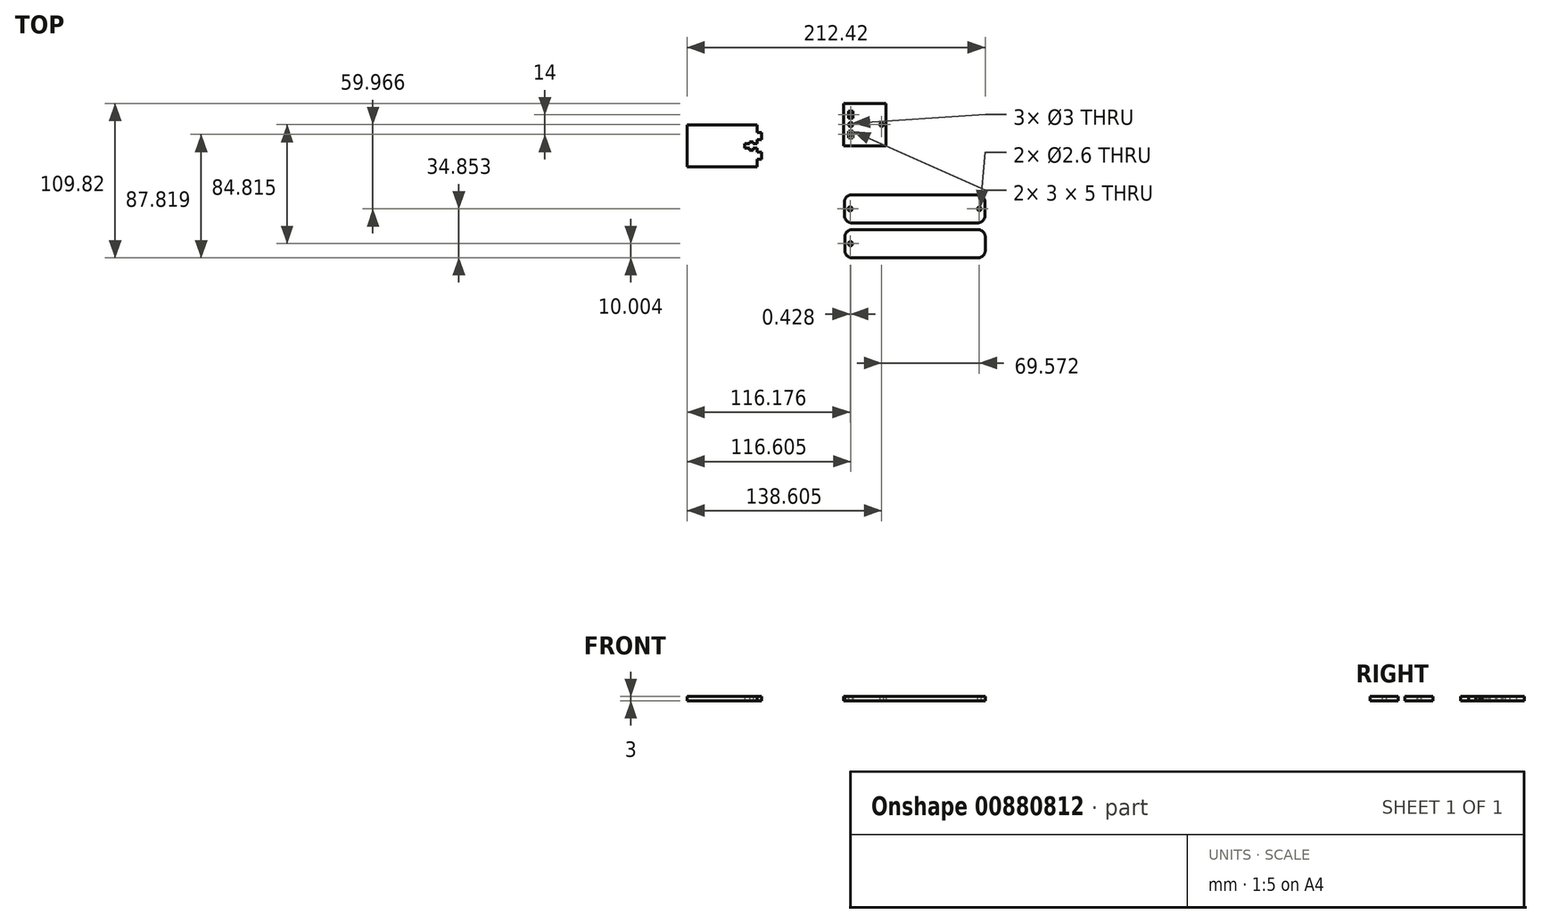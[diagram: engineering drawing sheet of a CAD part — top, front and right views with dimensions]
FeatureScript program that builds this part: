
annotation { "Feature Type Name" : "Feature", "Feature Type Description" : "" }
export const myFeature = defineFeature(function(context is Context, id is Id, definition is map)
    precondition{}
    {
        {
            var Q0;
            Q0=qCreatedBy(makeId("Top.planeOp"),FACE);
            var sketch = newSketch(context, id + "F0", { "sketchPlane" : qUnion([Q0])});
            skLineSegment(sketch, "E0", {"start": v(-41.94, 24.5) * mm, "end": v(-38.94, 24.5) * mm});
            skLineSegment(sketch, "E1", {"start": v(-38.94, 24.5) * mm, "end": v(-38.94, 19.5) * mm});
            skLineSegment(sketch, "E2", {"start": v(-38.94, 19.5) * mm, "end": v(-41.94, 19.5) * mm});
            skLineSegment(sketch, "E3", {"start": v(-41.94, 19.5) * mm, "end": v(-41.94, 16.5) * mm});
            skLineSegment(sketch, "E4", {"start": v(-41.94, 16.5) * mm, "end": v(-44.94, 16.5) * mm});
            skLineSegment(sketch, "E5", {"start": v(-44.94, 16.5) * mm, "end": v(-44.94, 18) * mm});
            skLineSegment(sketch, "E6", {"start": v(-44.94, 18) * mm, "end": v(-47.44, 18) * mm});
            skLineSegment(sketch, "E7", {"start": v(-47.44, 18) * mm, "end": v(-47.44, 16.5) * mm});
            skLineSegment(sketch, "E8", {"start": v(-47.44, 16.5) * mm, "end": v(-50.94, 16.5) * mm});
            skLineSegment(sketch, "E9", {"start": v(-50.94, 16.5) * mm, "end": v(-50.94, 13.5) * mm});
            skLineSegment(sketch, "E10", {"start": v(-50.94, 13.5) * mm, "end": v(-47.44, 13.5) * mm});
            skLineSegment(sketch, "E11", {"start": v(-47.44, 13.5) * mm, "end": v(-47.44, 12) * mm});
            skLineSegment(sketch, "E12", {"start": v(-47.44, 12) * mm, "end": v(-44.94, 12) * mm});
            skLineSegment(sketch, "E13", {"start": v(-44.94, 12) * mm, "end": v(-44.94, 13.5) * mm});
            skLineSegment(sketch, "E14", {"start": v(-44.94, 13.5) * mm, "end": v(-41.94, 13.5) * mm});
            skLineSegment(sketch, "E15", {"start": v(-41.94, 13.5) * mm, "end": v(-41.94, 10.5) * mm});
            skLineSegment(sketch, "E16", {"start": v(-41.94, 10.5) * mm, "end": v(-38.94, 10.5) * mm});
            skLineSegment(sketch, "E17", {"start": v(-38.94, 10.5) * mm, "end": v(-38.94, 5.5) * mm});
            skLineSegment(sketch, "E18", {"start": v(-38.94, 5.5) * mm, "end": v(-41.94, 5.5) * mm});
            skLineSegment(sketch, "E19.bottom", {"start": v(-91.94, 30) * mm, "end": v(-41.94, 30) * mm});
            skLineSegment(sketch, "E19.top", {"start": v(-91.94, 0) * mm, "end": v(-41.94, 0) * mm});
            skLineSegment(sketch, "E19.left", {"start": v(-91.94, 30) * mm, "end": v(-91.94, 0) * mm});
            skPoint(sketch, "E20", {"position": v(-41.94, 15) * mm});
            skPoint(sketch, "E20.positionSnap0", {"position": v(-50.94, 15) * mm});
            skPoint(sketch, "E21.positionSnap0", {"position": v(-91.94, 15) * mm});
            skLineSegment(sketch, "E22", {"start": v(-41.94, 5.5) * mm, "end": v(-41.94, 0) * mm});
            skLineSegment(sketch, "E23", {"start": v(-41.94, 30) * mm, "end": v(-41.94, 24.5) * mm});
            skSolve(sketch);
        }
        {
            var Q0;
            Q0=qCreatedBy(makeId("Top.planeOp"),FACE);
            var sketch = newSketch(context, id + "F1", { "sketchPlane" : qUnion([Q0])});
            skLineSegment(sketch, "E24.bottom", {"start": v(23.16, 39.69) * mm, "end": v(26.16, 39.69) * mm});
            skLineSegment(sketch, "E24.top", {"start": v(23.16, 34.69) * mm, "end": v(26.16, 34.69) * mm});
            skLineSegment(sketch, "E24.left", {"start": v(23.16, 39.69) * mm, "end": v(23.16, 34.69) * mm});
            skLineSegment(sketch, "E24.right", {"start": v(26.16, 39.69) * mm, "end": v(26.16, 34.69) * mm});
            skCircle(sketch, "E25", {"center": v(24.66, 30.19) * mm, "radius": 1.5 * mm});
            skPoint(sketch, "E26", {"position": v(24.66, 34.69) * mm});
            skLineSegment(sketch, "E27.bottom", {"start": v(23.16, 25.69) * mm, "end": v(26.16, 25.69) * mm});
            skLineSegment(sketch, "E27.top", {"start": v(23.16, 20.69) * mm, "end": v(26.16, 20.69) * mm});
            skLineSegment(sketch, "E27.left", {"start": v(23.16, 25.69) * mm, "end": v(23.16, 20.69) * mm});
            skLineSegment(sketch, "E27.right", {"start": v(26.16, 25.69) * mm, "end": v(26.16, 20.69) * mm});
            skPoint(sketch, "E28", {"position": v(24.66, 20.69) * mm});
            skLineSegment(sketch, "E29.bottom", {"start": v(19.66, 45.19) * mm, "end": v(49.66, 45.19) * mm});
            skLineSegment(sketch, "E29.top", {"start": v(19.66, 15.19) * mm, "end": v(49.66, 15.19) * mm});
            skLineSegment(sketch, "E29.left", {"start": v(19.66, 45.19) * mm, "end": v(19.66, 15.19) * mm});
            skLineSegment(sketch, "E29.right", {"start": v(49.66, 45.19) * mm, "end": v(49.66, 15.19) * mm});
            skPoint(sketch, "E30.positionSnap0", {"position": v(19.66, 30.19) * mm});
            skCircle(sketch, "E31", {"center": v(46.66, 30.19) * mm, "radius": 1.3 * mm});
            skPoint(sketch, "E32", {"position": v(49.66, 30.19) * mm});
            skSolve(sketch);
        }
        {
            var Q0;
            Q0=makeQuery(id+"F0.imprint","IMPRINT",FACE,{"disambiguationData":[TD([[makeQuery(id+"F0.imprint","IMPRINT",EDGE,{"derivedFrom":sQuery(id+"F0.wireOp",EDGE,"E0")}),-1.0]])]});
            extrude(context, id + "F2", {"entities" : qUnion([Q0]), "depth" : 3 * mm, "offsetDistance" : 25 * mm});
        }
        {
            var Q0;
            Q0=makeQuery(id+"F1.imprint","IMPRINT",FACE,{"disambiguationData":[TD([[makeQuery(id+"F1.imprint","IMPRINT",EDGE,{"derivedFrom":sQuery(id+"F1.wireOp",EDGE,"E24.bottom")}),1.0]])]});
            extrude(context, id + "F3", {"entities" : qUnion([Q0]), "depth" : 3 * mm, "offsetDistance" : 25 * mm});
        }
        {
            var Q0;
            Q0=qCreatedBy(makeId("Top.planeOp"),FACE);
            var sketch = newSketch(context, id + "F4", { "sketchPlane" : qUnion([Q0])});
            skLineSegment(sketch, "E33.bottom", {"start": v(25.24, -19.78) * mm, "end": v(115.24, -19.78) * mm});
            skLineSegment(sketch, "E33.top", {"start": v(25.24, -39.78) * mm, "end": v(115.24, -39.78) * mm});
            skLineSegment(sketch, "E33.left", {"start": v(20.24, -24.78) * mm, "end": v(20.24, -34.78) * mm});
            skLineSegment(sketch, "E33.right", {"start": v(120.24, -24.78) * mm, "end": v(120.24, -34.78) * mm});
            skCircle(sketch, "E34", {"center": v(24.24, -29.78) * mm, "radius": 1.5 * mm});
            skPoint(sketch, "E35", {"position": v(20.24, -29.78) * mm});
            skCircle(sketch, "E36", {"center": v(116.24, -29.78) * mm, "radius": 1.3 * mm});
            skPoint(sketch, "E37", {"position": v(120.24, -29.78) * mm});
            skLineSegment(sketch, "E38.bottom", {"start": v(25.48, -44.63) * mm, "end": v(115.48, -44.63) * mm});
            skLineSegment(sketch, "E38.top", {"start": v(25.48, -64.63) * mm, "end": v(115.48, -64.63) * mm});
            skLineSegment(sketch, "E38.left", {"start": v(20.48, -49.63) * mm, "end": v(20.48, -59.63) * mm});
            skLineSegment(sketch, "E38.right", {"start": v(120.48, -49.63) * mm, "end": v(120.48, -59.63) * mm});
            skCircle(sketch, "E39", {"center": v(24.48, -54.63) * mm, "radius": 1.5 * mm});
            skPoint(sketch, "E40", {"position": v(20.48, -54.63) * mm});
            skPoint(sketch, "E41.visualSharp", {"position": v(20.48, -44.63) * mm});
            skArc(sketch, "E41.filletArc", {"start": v(25.48, -44.63) * mm, "mid": v(21.95, -46.1) * mm, "end": v(20.48, -49.63) * mm});
            skPoint(sketch, "E42.visualSharp", {"position": v(20.48, -64.63) * mm});
            skArc(sketch, "E42.filletArc", {"start": v(20.48, -59.63) * mm, "mid": v(21.95, -63.16) * mm, "end": v(25.48, -64.63) * mm});
            skPoint(sketch, "E43.visualSharp", {"position": v(120.48, -44.63) * mm});
            skArc(sketch, "E43.filletArc", {"start": v(120.48, -49.63) * mm, "mid": v(119.02, -46.1) * mm, "end": v(115.48, -44.63) * mm});
            skPoint(sketch, "E44.visualSharp", {"position": v(120.48, -64.63) * mm});
            skArc(sketch, "E44.filletArc", {"start": v(115.48, -64.63) * mm, "mid": v(119.02, -63.16) * mm, "end": v(120.48, -59.63) * mm});
            skPoint(sketch, "E45.visualSharp", {"position": v(20.24, -19.78) * mm});
            skArc(sketch, "E45.filletArc", {"start": v(25.24, -19.78) * mm, "mid": v(21.7, -21.24) * mm, "end": v(20.24, -24.78) * mm});
            skPoint(sketch, "E46.visualSharp", {"position": v(20.24, -39.78) * mm});
            skArc(sketch, "E46.filletArc", {"start": v(20.24, -34.78) * mm, "mid": v(21.7, -38.31) * mm, "end": v(25.24, -39.78) * mm});
            skPoint(sketch, "E47.visualSharp", {"position": v(120.24, -19.78) * mm});
            skArc(sketch, "E47.filletArc", {"start": v(120.24, -24.78) * mm, "mid": v(118.77, -21.24) * mm, "end": v(115.24, -19.78) * mm});
            skPoint(sketch, "E48.visualSharp", {"position": v(120.24, -39.78) * mm});
            skArc(sketch, "E48.filletArc", {"start": v(115.24, -39.78) * mm, "mid": v(118.77, -38.31) * mm, "end": v(120.24, -34.78) * mm});
            skSolve(sketch);
        }
        {
            var Q0;
            Q0=makeQuery(id+"F4.imprint","IMPRINT",FACE,{"disambiguationData":[TD([[makeQuery(id+"F4.imprint","IMPRINT",EDGE,{"derivedFrom":sQuery(id+"F4.wireOp",EDGE,"E33.bottom")}),-1.0]])]});
            extrude(context, id + "F5", {"entities" : qUnion([Q0]), "depth" : 3 * mm, "offsetDistance" : 25 * mm});
        }
        {
            var Q0;
            Q0=makeQuery(id+"F4.imprint","IMPRINT",FACE,{"disambiguationData":[TD([[makeQuery(id+"F4.imprint","IMPRINT",EDGE,{"derivedFrom":sQuery(id+"F4.wireOp",EDGE,"E38.bottom")}),-1.0]])]});
            extrude(context, id + "F6", {"entities" : qUnion([Q0]), "depth" : 3 * mm, "offsetDistance" : 25 * mm});
        }
    });
